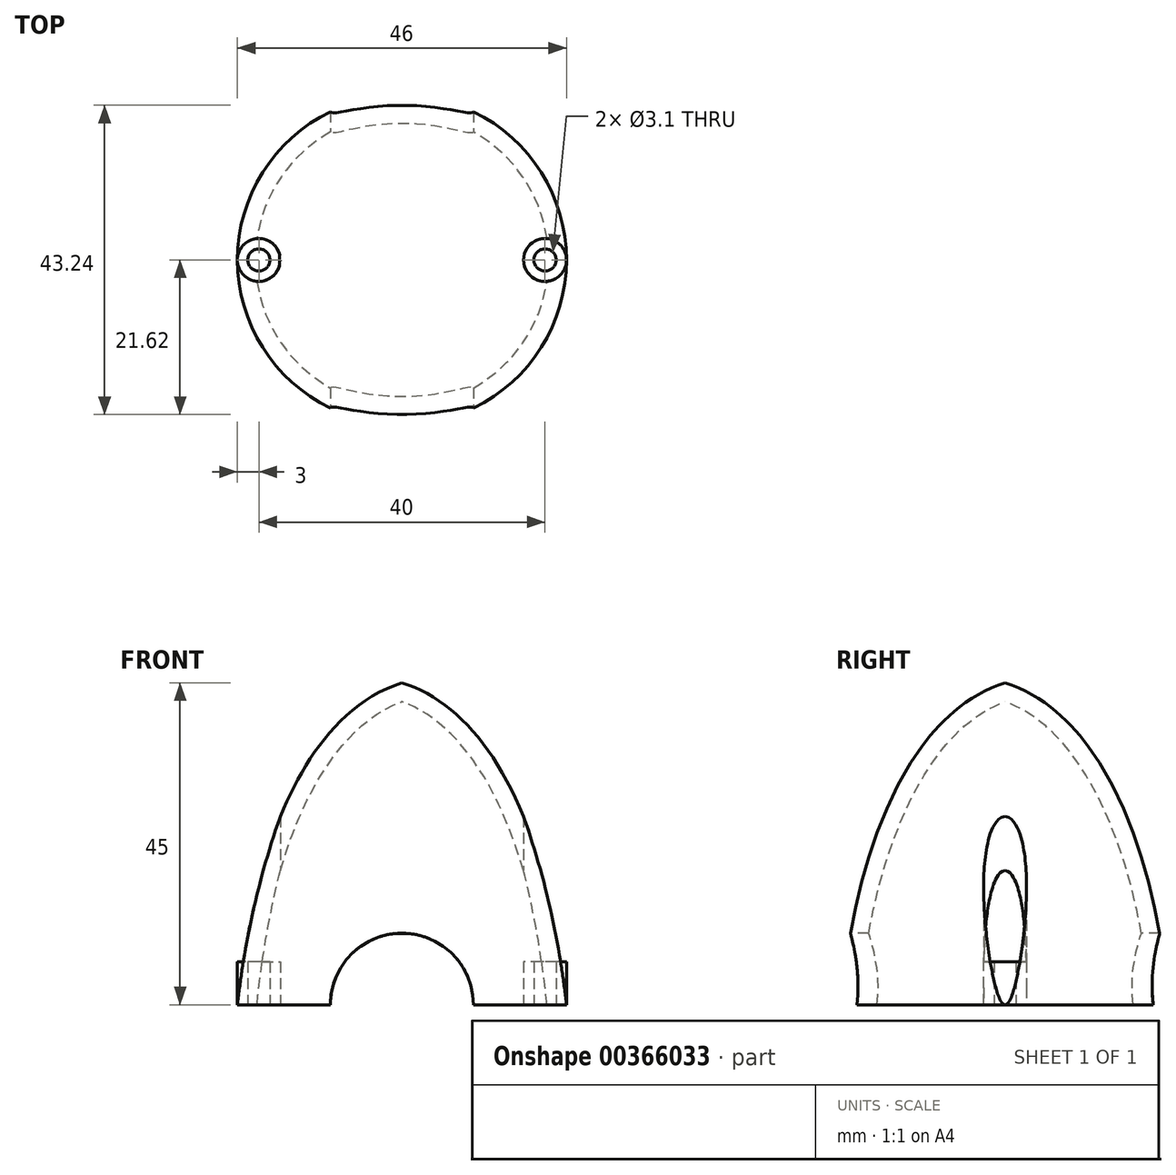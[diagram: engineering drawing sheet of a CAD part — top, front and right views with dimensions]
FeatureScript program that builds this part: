
annotation { "Feature Type Name" : "Feature", "Feature Type Description" : "" }
export const myFeature = defineFeature(function(context is Context, id is Id, definition is map)
    precondition{}
    {
        {
            var Q0;
            Q0=qCreatedBy(makeId("Front.planeOp"),FACE);
            var sketch = newSketch(context, id + "F0", { "sketchPlane" : qUnion([Q0])});
            skLineSegment(sketch, "E0", {"start": v(0, 0) * mm, "end": v(23, 0) * mm});
            skFitSpline(sketch, "E1", {"points": [v(23, 0) * mm, v(0, 45) * mm], "startDerivative": vector(-7.55, 76.93) * mm, "endDerivative": vector(-35.05, 10.73) * mm});
            skLineSegment(sketch, "E2", {"start": v(0, 0) * mm, "end": v(0, 45) * mm});
            skLineSegment(sketch, "E3", {"start": v(0, 63.88) * mm, "end": v(0, -31.1) * mm, "construction": true});
            skSolve(sketch);
        }
        {
            var Q0;
            Q0 = qSketchRegion(id + "F0", true);
            var Q1;
            Q1=sQuery(id+"F0.wireOp",EDGE,"E3");
            revolve(context, id + "F1", {"entities" : qUnion([Q0]), "axis" : qUnion([Q1]), "revolveType" : RevolveType.FULL});
        }
        {
            var Q0;
            Q0=makeQuery(id+"F1.opRevolve","SWEPT_FACE",FACE,{"disambiguationData":[OSD([sQuery(id+"F0.wireOp",EDGE,"E0")])]});
            shell(context, id + "F2", {"entities" : qUnion([Q0]), "thickness" : 2.5 * mm});
        }
        {
            var Q0;
            Q0=qCreatedBy(makeId("Top.planeOp"),FACE);
            var sketch = newSketch(context, id + "F3", { "sketchPlane" : qUnion([Q0])});
            skCircle(sketch, "E4", {"center": v(-20, 0) * mm, "radius": 3 * mm});
            skCircle(sketch, "E5", {"center": v(-20, 0) * mm, "radius": 1.55 * mm});
            skCircle(sketch, "E6.MirrorC", {"center": v(20, 0) * mm, "radius": 3 * mm});
            skCircle(sketch, "E7.MirrorC", {"center": v(20, 0) * mm, "radius": 1.55 * mm});
            skSolve(sketch);
        }
        {
            var Q0;
            Q0 = qSketchRegion(id + "F3", true);
            extrude(context, id + "F4", {"entities" : qUnion([Q0]), "operationType" : NewBodyOperationType.ADD, "depth" : 6 * mm});
        }
        {
            var Q0;
            {var subQ0=sQuery(id+"F3.wireOp",EDGE,"E4");Q0=makeQuery(id+"F4.boolean.opBoolean","SPLIT",FACE,{"disambiguationData":[TD([makeQuery(id+"F1.opRevolve","SWEPT_FACE",FACE,{"disambiguationData":[OSD([sQuery(id+"F0.wireOp",EDGE,"E1")])]})])],"derivedFrom":makeQuery(id+"F4.opExtrude","CAP_FACE",FACE,{"disambiguationData":[OSD([subQ0,sQuery(id+"F3.wireOp",EDGE,"E5")])],"isStart":false})});}
            var sketch = newSketch(context, id + "F5", { "sketchPlane" : qUnion([Q0])});
            skCircle(sketch, "E8", {"center": v(-20, 0) * mm, "radius": 3 * mm});
            skCircle(sketch, "E9.MirrorC", {"center": v(20, 0) * mm, "radius": 3 * mm});
            skSolve(sketch);
        }
        {
            var Q0;
            Q0 = qSketchRegion(id + "F5", true);
            extrude(context, id + "F6", {"entities" : qUnion([Q0]), "operationType" : NewBodyOperationType.REMOVE, "depth" : 25 * mm});
        }
        {
            var Q0;
            {var subQ0=sQuery(id+"F0.wireOp",EDGE,"E1");var subQ1=sQuery(id+"F3.wireOp",EDGE,"E4");var subQ3=sQuery(id+"F3.wireOp",EDGE,"E5");var subQ4=makeQuery(id+"F4.opExtrude","CAP_FACE",FACE,{"disambiguationData":[OSD([subQ1,subQ3])],"isStart":false});Q0=makeQuery(id+"F6.boolean.opBoolean","MERGE",FACE,{"derivedFrom":[makeQuery(id+"F4.boolean.opBoolean","SPLIT",FACE,{"disambiguationData":[TD([makeQuery(id+"F1.opRevolve","SWEPT_FACE",FACE,{"disambiguationData":[OSD([subQ0])]})])],"derivedFrom":subQ4}),makeQuery(id+"F4.boolean.opBoolean","SPLIT",FACE,{"disambiguationData":[TD([makeQuery(id+"F2.opShell","OFFSET_FACE",FACE,{"disambiguationData":[OSD([subQ0])]})])],"derivedFrom":subQ4}),makeQuery(id+"F6.opExtrude","CAP_FACE",FACE,{"disambiguationData":[OSD([sQuery(id+"F5.wireOp",EDGE,"E8")])],"isStart":true})]});}
            var sketch = newSketch(context, id + "F7", { "sketchPlane" : qUnion([Q0])});
            skCircle(sketch, "E10", {"center": v(-20, 0) * mm, "radius": 1.55 * mm});
            skCircle(sketch, "E11.MirrorC", {"center": v(20, 0) * mm, "radius": 1.55 * mm});
            skSolve(sketch);
        }
        {
            var Q0;
            Q0 = qSketchRegion(id + "F7", true);
            extrude(context, id + "F8", {"entities" : qUnion([Q0]), "operationType" : NewBodyOperationType.REMOVE, "oppositeDirection" : true, "depth" : 25 * mm});
        }
        {
            var Q0;
            Q0=qCreatedBy(makeId("Front.planeOp"),FACE);
            var sketch = newSketch(context, id + "F9", { "sketchPlane" : qUnion([Q0])});
            skArc(sketch, "E12", {"start": v(10, 0) * mm, "mid": v(0, 10) * mm, "end": v(-10, 0) * mm});
            skLineSegment(sketch, "E13", {"start": v(10, 0) * mm, "end": v(-10, 0) * mm});
            skSolve(sketch);
        }
        {
            var Q0;
            Q0 = qSketchRegion(id + "F9", true);
            extrude(context, id + "F10", {"entities" : qUnion([Q0]), "operationType" : NewBodyOperationType.REMOVE, "endBound" : BoundingType.SYMMETRIC, "oppositeDirection" : true, "depth" : 50 * mm});
        }
    });
